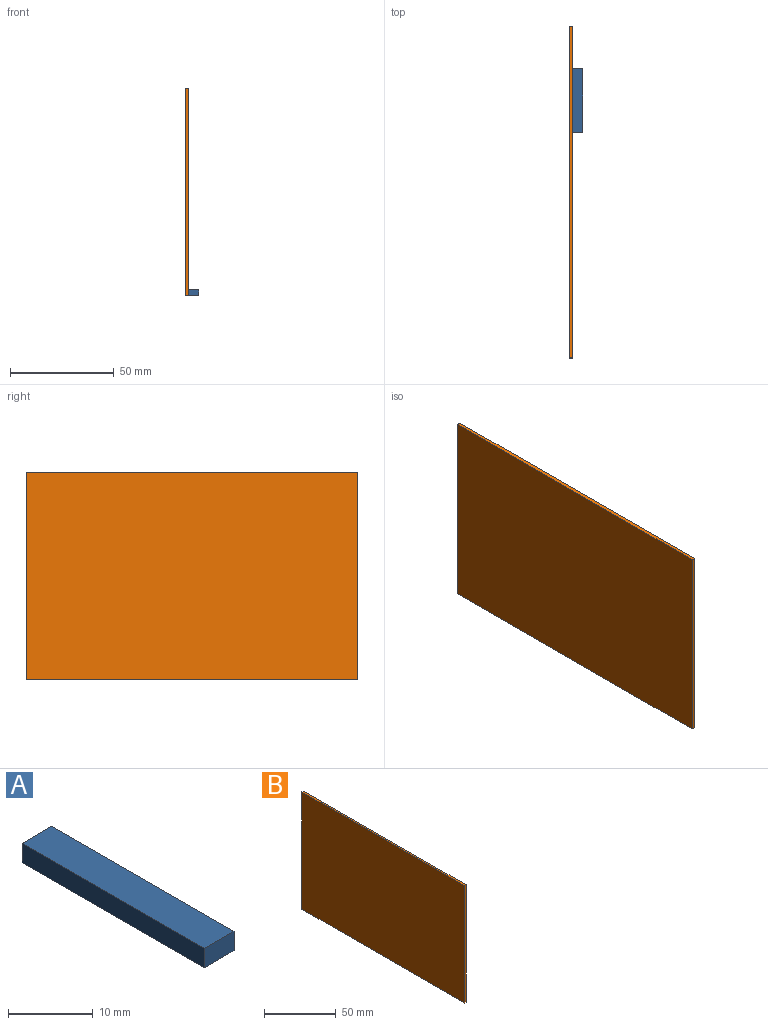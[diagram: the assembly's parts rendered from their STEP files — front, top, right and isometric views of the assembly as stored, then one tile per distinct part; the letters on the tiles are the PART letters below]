
ASSEMBLY  parts=2 mates=1
PART A: 6 faces, bbox 5x30.5x2.8 mm
  f0: plane 5x2.8mm, normal (0,1,0), area 14mm2, adj f1,f3,f4,f5
  f1: plane 30.48x2.8mm, normal (-1,0,0), area 85.3mm2, adj f0,f2,f4,f5
  f2: plane 5x2.8mm, normal (0,-1,0), area 14mm2, adj f1,f3,f4,f5
  f3: plane 30.48x2.8mm, normal (1,0,0), area 85.3mm2, adj f0,f2,f4,f5
  f4: plane 30.48x5mm, normal (0,0,1), area 152.4mm2, adj f0,f1,f2,f3
  f5: plane 30.48x5mm, normal (0,0,-1), area 152.4mm2, adj f0,f1,f2,f3
PART B: 6 faces, bbox 1.6x160x100 mm
  f0: plane 160x1.6mm, normal (0,0,1), area 256mm2, adj f1,f3,f4,f5
  f1: plane 100x1.6mm, normal (0,-1,0), area 160mm2, adj f0,f2,f4,f5
  f2: plane 160x1.6mm, normal (0,0,-1), area 256mm2, adj f1,f3,f4,f5
  f3: plane 100x1.6mm, normal (0,1,0), area 160mm2, adj f0,f2,f4,f5
  f4: plane 160x100mm, normal (1,0,0), area 16000mm2, adj f0,f1,f2,f3
  f5: plane 160x100mm, normal (-1,0,0), area 16000mm2, adj f0,f1,f2,f3
PLACE A t=(1.6,108.98,0)mm
PLACE B at identity
MATE fastened A.f1 <-> B.f4  axis (-1,0,0) through (1.6,139.46,0)mm
